FCSTD DOCUMENT  (FreeCAD 0.20RUnknown)
Label: DuschTuer
License: All rights reserved
LicenseURL: http://en.wikipedia.org/wiki/All_rights_reserved
objects: Sketcher::SketchObject×1, PartDesign::Body×1
note: 2 computed .brp shape members not serialized (recipe doc carries the construction recipe); baked Part::Feature solids carry a one-line shape summary decoded from their .brp

FEATURE [Sketcher::SketchObject] Sketch
  FullyConstrained = false
  MapMode = 5
  Support = -> [XY_Plane]
  sketch-geometry (10):
    g0: LineSegment StartX=0 StartY=0 StartZ=0 EndX=-64.3349 EndY=0 EndZ=0
    g1: LineSegment StartX=-64.3349 StartY=0 StartZ=0 EndX=-64.3349 EndY=5.50458 EndZ=0
    g2: LineSegment StartX=-64.3349 StartY=5.50458 StartZ=0 EndX=-10.8945 EndY=16.9725 EndZ=0
    g3: LineSegment StartX=-10.8945 StartY=16.9725 StartZ=0 EndX=-10.8945 EndY=30.9763 EndZ=0
    g4: LineSegment StartX=-10.8945 StartY=30.9763 StartZ=0 EndX=2.87415 EndY=38.9778 EndZ=0
    g5: LineSegment StartX=2.87415 StartY=38.9778 StartZ=0 EndX=29.0138 EndY=38.9778 EndZ=0
    g6: LineSegment StartX=29.0138 StartY=38.9778 StartZ=0 EndX=29.0138 EndY=32.9329 EndZ=0
    g7: LineSegment StartX=29.0138 StartY=32.9329 StartZ=0 EndX=12.4916 EndY=32.9329 EndZ=0
    g8: LineSegment StartX=12.4916 StartY=32.9329 StartZ=0 EndX=0 EndY=25.6735 EndZ=0
    g9: LineSegment StartX=0 StartY=25.6735 StartZ=0 EndX=0 EndY=0 EndZ=0
  constraints (19):
    c: Coincident(g-1,g0)
    c: PointOnObject(g0,g-1)
    c: Coincident(g0,g1)
    c: Vertical(g1)
    c: Coincident(g1,g2)
    c: Coincident(g2,g3)
    c: Vertical(g3)
    c: Coincident(g3,g4)
    c: Coincident(g4,g5)
    c: Horizontal(g5)
    c: Coincident(g5,g6)
    c: Coincident(g6,g7)
    c: Coincident(g7,g8)
    c: PointOnObject(g8,g-2)
    c: Coincident(g8,g9)
    c: Coincident(g9,g0)
    c: Vertical(g6)
    c: Horizontal(g7)
    c: Parallel(g8,g4)
FEATURE [PartDesign::Body] Body  label="Guide"
  Group = -> [Sketch]
  Origin = -> Origin
